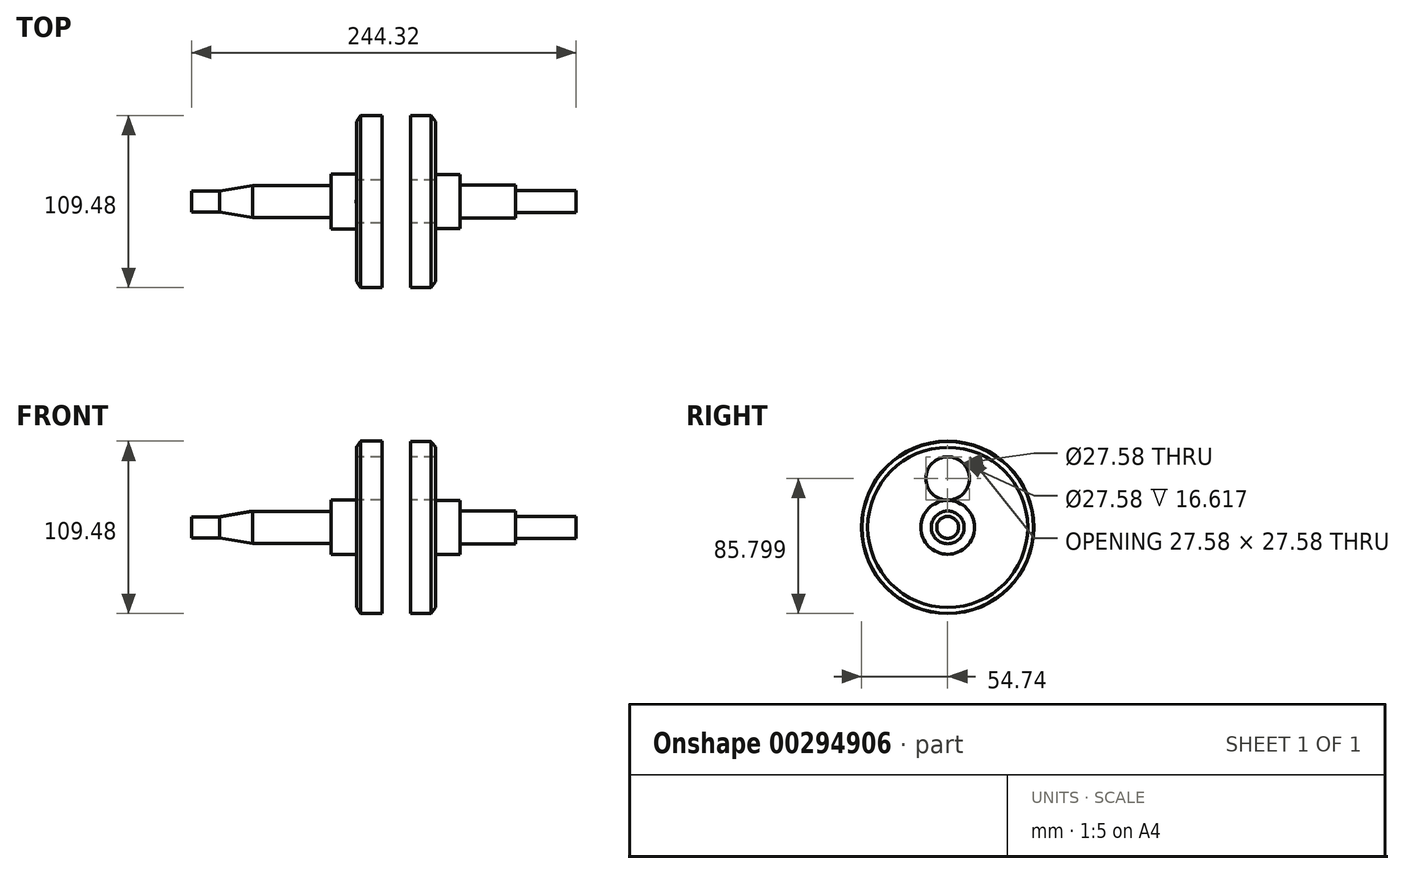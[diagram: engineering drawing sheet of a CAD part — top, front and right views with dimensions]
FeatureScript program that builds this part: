
annotation { "Feature Type Name" : "Feature", "Feature Type Description" : "" }
export const myFeature = defineFeature(function(context is Context, id is Id, definition is map)
    precondition{}
    {
        {
            var Q0;
            Q0=qCreatedBy(makeId("Front.planeOp"),FACE);
            var sketch = newSketch(context, id + "F0", { "sketchPlane" : qUnion([Q0])});
            skLineSegment(sketch, "E0", {"start": v(-456.62, -19.36) * mm, "end": v(-335.47, -19.36) * mm});
            skLineSegment(sketch, "E1", {"start": v(-456.62, -19.36) * mm, "end": v(-456.62, -12.66) * mm});
            skLineSegment(sketch, "E2", {"start": v(-438.76, -12.66) * mm, "end": v(-417.76, -9.08) * mm});
            skLineSegment(sketch, "E3", {"start": v(-417.76, -9.08) * mm, "end": v(-367.97, -9.08) * mm});
            skLineSegment(sketch, "E4", {"start": v(-367.97, -9.08) * mm, "end": v(-367.97, -2.04) * mm});
            skLineSegment(sketch, "E5", {"start": v(-351.9, -2.04) * mm, "end": v(-351.9, 31.58) * mm});
            skLineSegment(sketch, "E6", {"start": v(-351.9, 31.58) * mm, "end": v(-349.26, 35.38) * mm});
            skLineSegment(sketch, "E7", {"start": v(-349.26, 35.38) * mm, "end": v(-335.47, 35.38) * mm});
            skLineSegment(sketch, "E8", {"start": v(-335.47, 35.38) * mm, "end": v(-335.47, -19.36) * mm});
            skLineSegment(sketch, "E9", {"start": v(-367.97, -2.04) * mm, "end": v(-351.9, -2.04) * mm});
            skLineSegment(sketch, "E10", {"start": v(-456.62, -12.66) * mm, "end": v(-438.76, -12.66) * mm});
            skLineSegment(sketch, "E11", {"start": v(-212.3, -19.36) * mm, "end": v(-212.3, -12.38) * mm});
            skLineSegment(sketch, "E12", {"start": v(-212.3, -12.38) * mm, "end": v(-250.77, -12.38) * mm});
            skLineSegment(sketch, "E13", {"start": v(-250.77, -12.38) * mm, "end": v(-250.77, -8.93) * mm});
            skLineSegment(sketch, "E14", {"start": v(-250.77, -8.93) * mm, "end": v(-285.98, -8.93) * mm});
            skLineSegment(sketch, "E15", {"start": v(-285.98, -8.93) * mm, "end": v(-285.98, -2.29) * mm});
            skLineSegment(sketch, "E16", {"start": v(-285.98, -2.29) * mm, "end": v(-301.5, -2.29) * mm});
            skLineSegment(sketch, "E17", {"start": v(-301.5, -2.29) * mm, "end": v(-301.5, 31.44) * mm});
            skLineSegment(sketch, "E18", {"start": v(-301.5, 31.44) * mm, "end": v(-304.45, 35.14) * mm});
            skLineSegment(sketch, "E19", {"start": v(-304.45, 35.14) * mm, "end": v(-317.5, 35.14) * mm});
            skLineSegment(sketch, "E20", {"start": v(-317.5, 35.14) * mm, "end": v(-317.5, -19.36) * mm});
            skLineSegment(sketch, "E21.trimOffspring", {"start": v(-317.5, -19.36) * mm, "end": v(-212.3, -19.36) * mm});
            skLineSegment(sketch, "E22", {"start": v(-301.5, 11.7) * mm, "end": v(-301.5, 25.07) * mm});
            skLineSegment(sketch, "E23", {"start": v(-351.9, 25.07) * mm, "end": v(-351.9, 11.7) * mm});
            skSolve(sketch);
        }
        {
            var Q0;
            Q0=makeQuery(id+"F0.imprint","IMPRINT",FACE,{"disambiguationData":[TD([[makeQuery(id+"F0.imprint","IMPRINT",EDGE,{"derivedFrom":sQuery(id+"F0.wireOp",EDGE,"E0")}),1.0]])]});
            var Q1;
            Q1=sQuery(id+"F0.wireOp",EDGE,"E0");
            revolve(context, id + "F1", {"entities" : qUnion([Q0]), "axis" : qUnion([Q1]), "revolveType" : RevolveType.FULL});
        }
        {
            var Q0;
            Q0=makeQuery(id+"F0.imprint","IMPRINT",FACE,{"disambiguationData":[TD([[makeQuery(id+"F0.imprint","IMPRINT",EDGE,{"derivedFrom":sQuery(id+"F0.wireOp",EDGE,"E11")}),1.0]])]});
            var Q1;
            Q1=sQuery(id+"F0.wireOp",EDGE,"E21.trimOffspring");
            revolve(context, id + "F2", {"entities" : qUnion([Q0]), "axis" : qUnion([Q1]), "revolveType" : RevolveType.FULL});
        }
        {
            var Q0;
            Q0=qCreatedBy(makeId("Front.planeOp"),FACE);
            var sketch = newSketch(context, id + "F3", { "sketchPlane" : qUnion([Q0])});
            skLineSegment(sketch, "E24", {"start": v(-352.09, 11.7) * mm, "end": v(-300.7, 11.7) * mm});
            skLineSegment(sketch, "E25", {"start": v(-300.7, 11.7) * mm, "end": v(-300.7, 25.49) * mm});
            skLineSegment(sketch, "E26", {"start": v(-300.7, 25.49) * mm, "end": v(-352.09, 25.49) * mm});
            skLineSegment(sketch, "E27", {"start": v(-352.09, 25.49) * mm, "end": v(-352.09, 11.7) * mm});
            skSolve(sketch);
        }
        {
            var Q0;
            Q0=makeQuery(id+"F3.imprint","IMPRINT",FACE,{"disambiguationData":[TD([[makeQuery(id+"F3.imprint","IMPRINT",EDGE,{"derivedFrom":sQuery(id+"F3.wireOp",EDGE,"E24")}),1.0]])]});
            var Q1;
            Q1=sQuery(id+"F3.wireOp",EDGE,"E24");
            revolve(context, id + "F4", {"entities" : qUnion([Q0]), "axis" : qUnion([Q1]), "revolveType" : RevolveType.FULL});
        }
        {
            var Q0;
            Q0=makeQuery(id+"F4.opRevolve","SWEPT_BODY",BODY,{"disambiguationData":[OSD([sQuery(id+"F3.wireOp",EDGE,"E24"),sQuery(id+"F3.wireOp",EDGE,"E25"),sQuery(id+"F3.wireOp",EDGE,"E26"),sQuery(id+"F3.wireOp",EDGE,"E27")])]});
            var Q1;
            Q1=makeQuery(id+"F1.opRevolve","SWEPT_BODY",BODY,{"disambiguationData":[OSD([sQuery(id+"F0.wireOp",EDGE,"E0"),sQuery(id+"F0.wireOp",EDGE,"E1"),sQuery(id+"F0.wireOp",EDGE,"E2"),sQuery(id+"F0.wireOp",EDGE,"E3"),sQuery(id+"F0.wireOp",EDGE,"E4"),sQuery(id+"F0.wireOp",EDGE,"E5"),sQuery(id+"F0.wireOp",EDGE,"E6"),sQuery(id+"F0.wireOp",EDGE,"E7"),sQuery(id+"F0.wireOp",EDGE,"E8"),sQuery(id+"F0.wireOp",EDGE,"E9"),sQuery(id+"F0.wireOp",EDGE,"E10"),sQuery(id+"F0.wireOp",EDGE,"E23")])]});
            var Q2;
            Q2=makeQuery(id+"F2.opRevolve","SWEPT_BODY",BODY,{"disambiguationData":[OSD([sQuery(id+"F0.wireOp",EDGE,"E11"),sQuery(id+"F0.wireOp",EDGE,"E12"),sQuery(id+"F0.wireOp",EDGE,"E13"),sQuery(id+"F0.wireOp",EDGE,"E14"),sQuery(id+"F0.wireOp",EDGE,"E15"),sQuery(id+"F0.wireOp",EDGE,"E16"),sQuery(id+"F0.wireOp",EDGE,"E17"),sQuery(id+"F0.wireOp",EDGE,"E18"),sQuery(id+"F0.wireOp",EDGE,"E19"),sQuery(id+"F0.wireOp",EDGE,"E20"),sQuery(id+"F0.wireOp",EDGE,"E21.trimOffspring"),sQuery(id+"F0.wireOp",EDGE,"E22")])]});
            booleanBodies(context, id + "F5", {"operationType" : BooleanOperationType.SUBTRACTION, "tools" : qUnion([Q0]), "targets" : qUnion([Q1, Q2])});
        }
    });
